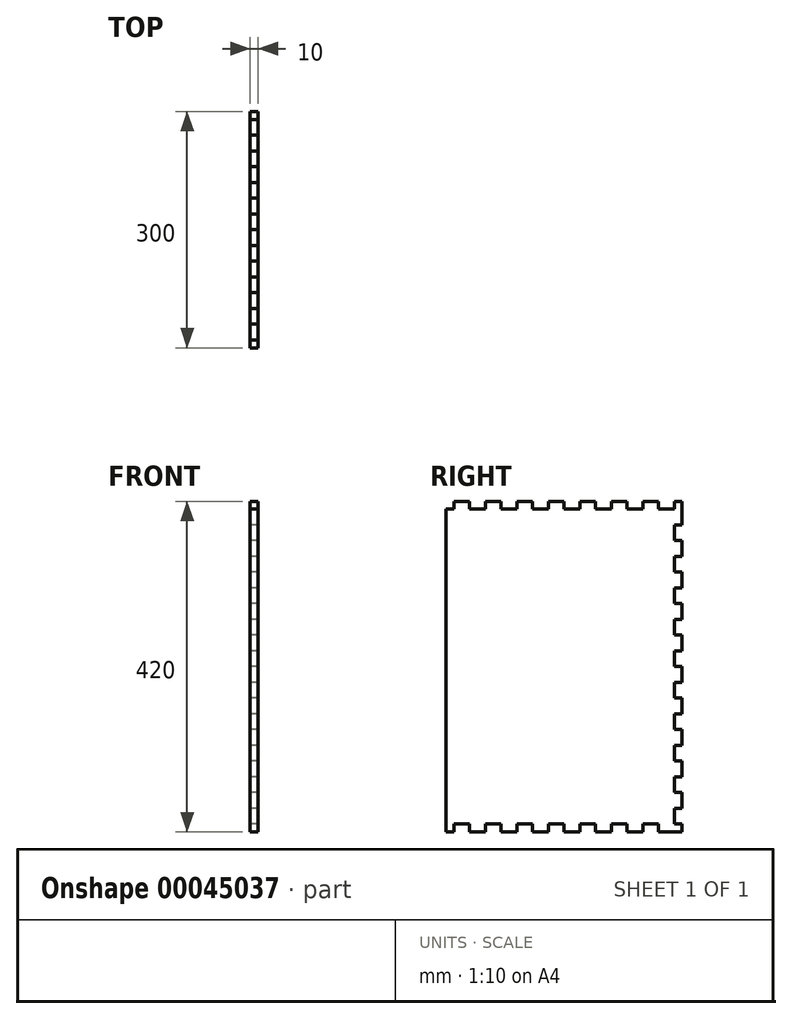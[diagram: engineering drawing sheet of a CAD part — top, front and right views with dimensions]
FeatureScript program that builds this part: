
annotation { "Feature Type Name" : "Feature", "Feature Type Description" : "" }
export const myFeature = defineFeature(function(context is Context, id is Id, definition is map)
    precondition{}
    {
        {
            var Q0;
            Q0=qCreatedBy(makeId("Right.planeOp"),FACE);
            var sketch = newSketch(context, id + "F0", { "sketchPlane" : qUnion([Q0])});
            skLineSegment(sketch, "E0.bottom", {"start": v(0, 0) * mm, "end": v(300, 0) * mm, "construction": true});
            skLineSegment(sketch, "E0.top", {"start": v(0, 420) * mm, "end": v(300, 420) * mm, "construction": true});
            skLineSegment(sketch, "E0.left", {"start": v(0, 0) * mm, "end": v(0, 420) * mm, "construction": true});
            skLineSegment(sketch, "E0.right", {"start": v(300, 0) * mm, "end": v(300, 420) * mm, "construction": true});
            skLineSegment(sketch, "E1", {"start": v(0, 0) * mm, "end": v(0, 410) * mm});
            skLineSegment(sketch, "E2", {"start": v(0, 410) * mm, "end": v(10, 410) * mm});
            skLineSegment(sketch, "E3", {"start": v(10, 410) * mm, "end": v(10, 420) * mm});
            skLineSegment(sketch, "E4", {"start": v(10, 420) * mm, "end": v(30.07, 420) * mm});
            skLineSegment(sketch, "E5", {"start": v(0, 410) * mm, "end": v(300, 410) * mm, "construction": true});
            skLineSegment(sketch, "E6", {"start": v(30.07, 420) * mm, "end": v(30.07, 410) * mm});
            skLineSegment(sketch, "E7", {"start": v(30.07, 410) * mm, "end": v(50, 410) * mm});
            skLineSegment(sketch, "E8", {"start": v(50, 410) * mm, "end": v(50, 420) * mm});
            skLineSegment(sketch, "E9", {"start": v(50, 420) * mm, "end": v(70.07, 420) * mm});
            skLineSegment(sketch, "E10", {"start": v(70.07, 420) * mm, "end": v(70.07, 410) * mm});
            skLineSegment(sketch, "E11", {"start": v(70.07, 410) * mm, "end": v(90, 410) * mm});
            skLineSegment(sketch, "E12", {"start": v(90, 410) * mm, "end": v(90, 420) * mm});
            skLineSegment(sketch, "E13", {"start": v(90, 420) * mm, "end": v(110.07, 420) * mm});
            skLineSegment(sketch, "E14", {"start": v(110.07, 420) * mm, "end": v(110.07, 410) * mm});
            skLineSegment(sketch, "E15", {"start": v(110.07, 410) * mm, "end": v(130, 410) * mm});
            skLineSegment(sketch, "E16", {"start": v(130, 410) * mm, "end": v(130, 420) * mm});
            skLineSegment(sketch, "E17", {"start": v(130, 420) * mm, "end": v(150.07, 420) * mm});
            skLineSegment(sketch, "E18", {"start": v(150.07, 420) * mm, "end": v(150.07, 410) * mm});
            skLineSegment(sketch, "E19", {"start": v(150.07, 410) * mm, "end": v(170, 410) * mm});
            skLineSegment(sketch, "E20", {"start": v(170, 410) * mm, "end": v(170, 420) * mm});
            skLineSegment(sketch, "E21", {"start": v(170, 420) * mm, "end": v(190.07, 420) * mm});
            skLineSegment(sketch, "E22", {"start": v(190.07, 420) * mm, "end": v(190.07, 410) * mm});
            skLineSegment(sketch, "E23", {"start": v(190.07, 410) * mm, "end": v(210, 410) * mm});
            skLineSegment(sketch, "E24", {"start": v(210, 410) * mm, "end": v(210, 420) * mm});
            skLineSegment(sketch, "E25", {"start": v(210, 420) * mm, "end": v(230.07, 420) * mm});
            skLineSegment(sketch, "E26", {"start": v(230.07, 420) * mm, "end": v(230.07, 410) * mm});
            skLineSegment(sketch, "E27", {"start": v(230.07, 410) * mm, "end": v(250, 410) * mm});
            skLineSegment(sketch, "E28", {"start": v(250, 410) * mm, "end": v(250, 420) * mm});
            skLineSegment(sketch, "E29", {"start": v(250, 420) * mm, "end": v(270.07, 420) * mm});
            skLineSegment(sketch, "E30", {"start": v(270.07, 420) * mm, "end": v(270.07, 410) * mm});
            skLineSegment(sketch, "E31", {"start": v(270.07, 410) * mm, "end": v(290, 410) * mm});
            skLineSegment(sketch, "E32", {"start": v(290, 410) * mm, "end": v(290, 420) * mm});
            skLineSegment(sketch, "E33", {"start": v(290, 420) * mm, "end": v(300, 420) * mm});
            skLineSegment(sketch, "E34", {"start": v(290, 420) * mm, "end": v(290, 0) * mm, "construction": true});
            skLineSegment(sketch, "E35", {"start": v(0, 10) * mm, "end": v(300, 10) * mm, "construction": true});
            skLineSegment(sketch, "E36", {"start": v(0, 0) * mm, "end": v(10, 0) * mm});
            skLineSegment(sketch, "E37", {"start": v(10, 0) * mm, "end": v(10, 10) * mm});
            skLineSegment(sketch, "E38", {"start": v(10, 10) * mm, "end": v(29.93, 10) * mm});
            skLineSegment(sketch, "E39", {"start": v(29.93, 10) * mm, "end": v(29.93, 0) * mm});
            skLineSegment(sketch, "E40", {"start": v(29.93, 0) * mm, "end": v(50, 0) * mm});
            skLineSegment(sketch, "E41", {"start": v(50, 0) * mm, "end": v(50, 10) * mm});
            skLineSegment(sketch, "E42", {"start": v(50, 10) * mm, "end": v(69.92, 10) * mm});
            skLineSegment(sketch, "E43", {"start": v(69.92, 10) * mm, "end": v(69.92, 0) * mm});
            skLineSegment(sketch, "E44", {"start": v(189.92, 10) * mm, "end": v(189.92, 0) * mm});
            skLineSegment(sketch, "E45", {"start": v(300, 420) * mm, "end": v(300, 389.93) * mm});
            skLineSegment(sketch, "E46", {"start": v(300, 389.93) * mm, "end": v(290, 389.93) * mm});
            skLineSegment(sketch, "E47", {"start": v(290, 389.93) * mm, "end": v(290, 370) * mm});
            skLineSegment(sketch, "E48", {"start": v(290, 370) * mm, "end": v(300, 370) * mm});
            skLineSegment(sketch, "E49", {"start": v(300, 370) * mm, "end": v(300, 349.93) * mm});
            skLineSegment(sketch, "E50", {"start": v(300, 349.93) * mm, "end": v(290, 349.93) * mm});
            skLineSegment(sketch, "E51", {"start": v(290, 349.93) * mm, "end": v(290, 330) * mm});
            skLineSegment(sketch, "E52", {"start": v(290, 330) * mm, "end": v(300, 330) * mm});
            skLineSegment(sketch, "E53", {"start": v(300, 330) * mm, "end": v(300, 309.93) * mm});
            skLineSegment(sketch, "E54", {"start": v(300, 309.93) * mm, "end": v(290, 309.93) * mm});
            skLineSegment(sketch, "E55", {"start": v(290, 309.93) * mm, "end": v(290, 290) * mm});
            skLineSegment(sketch, "E56", {"start": v(290, 290) * mm, "end": v(300, 290) * mm});
            skLineSegment(sketch, "E57", {"start": v(300, 290) * mm, "end": v(300, 269.92) * mm});
            skLineSegment(sketch, "E58", {"start": v(300, 269.92) * mm, "end": v(290, 269.92) * mm});
            skLineSegment(sketch, "E59", {"start": v(290, 269.92) * mm, "end": v(290, 250) * mm});
            skLineSegment(sketch, "E60", {"start": v(290, 250) * mm, "end": v(300, 250) * mm});
            skLineSegment(sketch, "E61", {"start": v(300, 250) * mm, "end": v(300, 229.92) * mm});
            skLineSegment(sketch, "E62", {"start": v(300, 229.92) * mm, "end": v(290, 229.92) * mm});
            skLineSegment(sketch, "E63", {"start": v(290, 229.92) * mm, "end": v(290, 210) * mm});
            skLineSegment(sketch, "E64", {"start": v(290, 210) * mm, "end": v(300, 210) * mm});
            skLineSegment(sketch, "E65", {"start": v(300, 210) * mm, "end": v(300, 189.92) * mm});
            skLineSegment(sketch, "E66", {"start": v(300, 189.92) * mm, "end": v(290, 189.92) * mm});
            skLineSegment(sketch, "E67", {"start": v(290, 189.92) * mm, "end": v(290, 170) * mm});
            skLineSegment(sketch, "E68", {"start": v(290, 170) * mm, "end": v(300, 170) * mm});
            skLineSegment(sketch, "E69", {"start": v(300, 170) * mm, "end": v(300, 149.92) * mm});
            skLineSegment(sketch, "E70", {"start": v(300, 149.92) * mm, "end": v(290, 149.92) * mm});
            skLineSegment(sketch, "E71", {"start": v(290, 149.92) * mm, "end": v(290, 130) * mm});
            skLineSegment(sketch, "E72", {"start": v(290, 130) * mm, "end": v(300, 130) * mm});
            skLineSegment(sketch, "E73", {"start": v(300, 130) * mm, "end": v(300, 109.92) * mm});
            skLineSegment(sketch, "E74", {"start": v(300, 109.92) * mm, "end": v(290, 109.92) * mm});
            skLineSegment(sketch, "E75", {"start": v(290, 109.92) * mm, "end": v(290, 90) * mm});
            skLineSegment(sketch, "E76", {"start": v(290, 90) * mm, "end": v(300, 90) * mm});
            skLineSegment(sketch, "E77", {"start": v(300, 90) * mm, "end": v(300, 69.92) * mm});
            skLineSegment(sketch, "E78", {"start": v(300, 69.92) * mm, "end": v(290, 69.92) * mm});
            skLineSegment(sketch, "E79", {"start": v(290, 69.92) * mm, "end": v(290, 50) * mm});
            skLineSegment(sketch, "E80", {"start": v(290, 50) * mm, "end": v(300, 50) * mm});
            skLineSegment(sketch, "E81", {"start": v(300, 50) * mm, "end": v(300, 29.92) * mm});
            skLineSegment(sketch, "E82", {"start": v(300, 29.92) * mm, "end": v(290, 29.92) * mm});
            skLineSegment(sketch, "E83", {"start": v(290, 29.92) * mm, "end": v(290, 10) * mm});
            skLineSegment(sketch, "E84", {"start": v(290, 10) * mm, "end": v(300, 10) * mm});
            skLineSegment(sketch, "E85", {"start": v(300, 10) * mm, "end": v(300, 0) * mm});
            skLineSegment(sketch, "E86", {"start": v(300, 0) * mm, "end": v(269.93, 0) * mm});
            skLineSegment(sketch, "E87", {"start": v(269.93, 0) * mm, "end": v(269.93, 10) * mm});
            skLineSegment(sketch, "E88", {"start": v(269.93, 10) * mm, "end": v(250, 10) * mm});
            skLineSegment(sketch, "E89", {"start": v(250, 10) * mm, "end": v(250, 0) * mm});
            skLineSegment(sketch, "E90", {"start": v(250, 0) * mm, "end": v(229.92, 0) * mm});
            skLineSegment(sketch, "E91", {"start": v(229.92, 0) * mm, "end": v(229.92, 10) * mm});
            skLineSegment(sketch, "E92", {"start": v(229.92, 10) * mm, "end": v(210, 10) * mm});
            skLineSegment(sketch, "E93", {"start": v(210, 10) * mm, "end": v(210, 0) * mm});
            skLineSegment(sketch, "E94", {"start": v(210, 0) * mm, "end": v(189.92, 0) * mm});
            skLineSegment(sketch, "E95", {"start": v(189.92, 10) * mm, "end": v(170, 10) * mm});
            skLineSegment(sketch, "E96", {"start": v(170, 10) * mm, "end": v(170, 0) * mm});
            skLineSegment(sketch, "E97", {"start": v(170, 0) * mm, "end": v(149.92, 0) * mm});
            skLineSegment(sketch, "E98", {"start": v(149.92, 0) * mm, "end": v(149.92, 10) * mm});
            skLineSegment(sketch, "E99", {"start": v(149.92, 10) * mm, "end": v(130, 10) * mm});
            skLineSegment(sketch, "E100", {"start": v(130, 10) * mm, "end": v(130, 0) * mm});
            skLineSegment(sketch, "E101", {"start": v(130, 0) * mm, "end": v(109.92, 0) * mm});
            skLineSegment(sketch, "E102", {"start": v(109.92, 0) * mm, "end": v(109.92, 10) * mm});
            skLineSegment(sketch, "E103", {"start": v(109.92, 10) * mm, "end": v(90, 10) * mm});
            skLineSegment(sketch, "E104", {"start": v(90, 10) * mm, "end": v(90, 0) * mm});
            skLineSegment(sketch, "E105", {"start": v(90, 0) * mm, "end": v(69.92, 0) * mm});
            skSolve(sketch);
        }
        {
            var Q0;
            Q0 = qSketchRegion(id + "F0", true);
            extrude(context, id + "F1", {"entities" : qUnion([Q0]), "depth" : 10 * mm});
        }
    });
